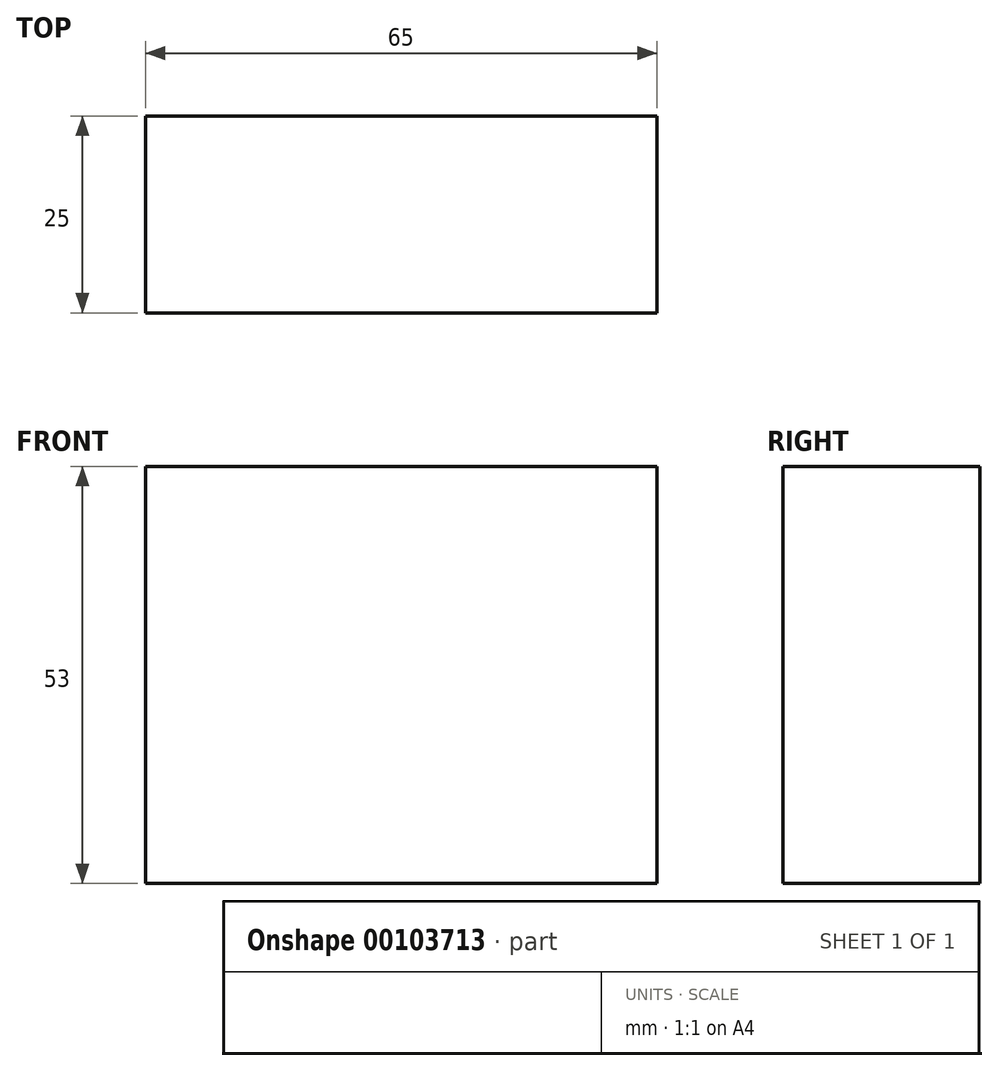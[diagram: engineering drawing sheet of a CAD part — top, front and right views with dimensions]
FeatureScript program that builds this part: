
annotation { "Feature Type Name" : "Feature", "Feature Type Description" : "" }
export const myFeature = defineFeature(function(context is Context, id is Id, definition is map)
    precondition{}
    {
        {
            var Q0;
            Q0=qCreatedBy(makeId("Front.planeOp"),FACE);
            var sketch = newSketch(context, id + "F0", { "sketchPlane" : qUnion([Q0])});
            skLineSegment(sketch, "E0.bottom", {"start": v(-32.5, 26.5) * mm, "end": v(32.5, 26.5) * mm});
            skLineSegment(sketch, "E0.top", {"start": v(-32.5, -26.5) * mm, "end": v(32.5, -26.5) * mm});
            skLineSegment(sketch, "E0.left", {"start": v(-32.5, 26.5) * mm, "end": v(-32.5, -26.5) * mm});
            skLineSegment(sketch, "E0.right", {"start": v(32.5, 26.5) * mm, "end": v(32.5, -26.5) * mm});
            skPoint(sketch, "E0.middle", {"position": v(0, 0) * mm});
            skSolve(sketch);
        }
        {
            var Q0;
            Q0=makeQuery(id+"F0.imprint","IMPRINT",FACE,{"disambiguationData":[TD([[makeQuery(id+"F0.imprint","IMPRINT",EDGE,{"derivedFrom":sQuery(id+"F0.wireOp",EDGE,"E0.bottom")}),-1.0]])]});
            extrude(context, id + "F1", {"entities" : qUnion([Q0]), "depth" : 25 * mm});
        }
    });
